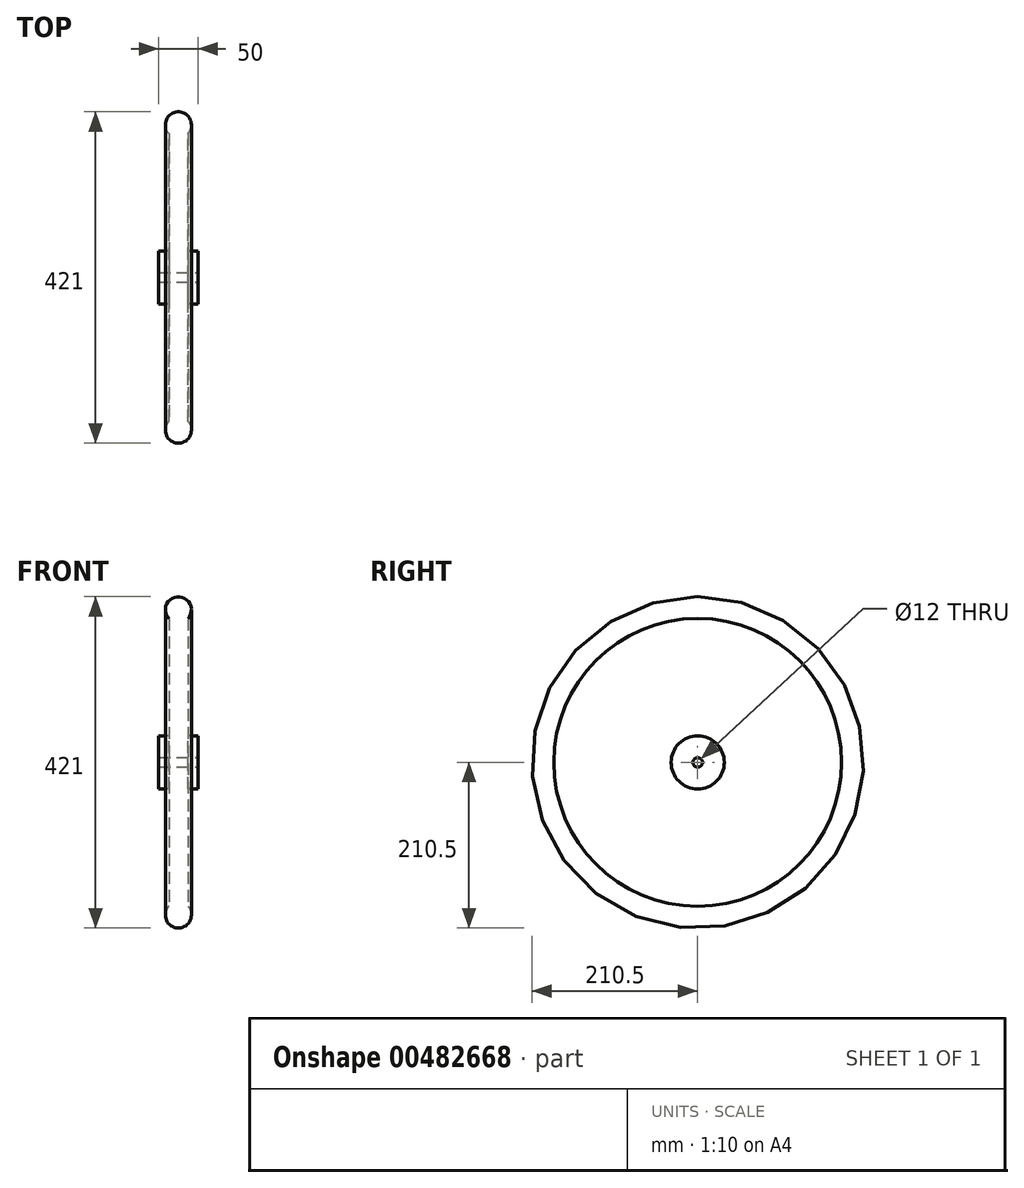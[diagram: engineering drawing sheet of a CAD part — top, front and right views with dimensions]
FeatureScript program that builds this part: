
annotation { "Feature Type Name" : "Feature", "Feature Type Description" : "" }
export const myFeature = defineFeature(function(context is Context, id is Id, definition is map)
    precondition{}
    {
        {
            var Q0;
            Q0=qCreatedBy(makeId("Front.planeOp"),FACE);
            var sketch = newSketch(context, id + "F0", { "sketchPlane" : qUnion([Q0])});
            skArc(sketch, "E0", {"start": v(12.11, 182.8) * mm, "mid": v(0, 210.5) * mm, "end": v(-12.11, 182.8) * mm});
            skLineSegment(sketch, "E1.top", {"start": v(-12.11, 0) * mm, "end": v(12.11, 0) * mm});
            skLineSegment(sketch, "E1.left", {"start": v(-12.11, 182.8) * mm, "end": v(-12.11, 0) * mm});
            skLineSegment(sketch, "E1.right", {"start": v(12.11, 182.8) * mm, "end": v(12.11, 0) * mm});
            skSolve(sketch);
        }
        {
            var Q0;
            Q0=makeQuery(id+"F0.imprint","IMPRINT",FACE,{"disambiguationData":[TD([[makeQuery(id+"F0.imprint","IMPRINT",EDGE,{"derivedFrom":sQuery(id+"F0.wireOp",EDGE,"E0")}),1.0]])]});
            var Q1;
            Q1=sQuery(id+"F0.wireOp",EDGE,"E1.top");
            revolve(context, id + "F1", {"entities" : qUnion([Q0]), "axis" : qUnion([Q1]), "revolveType" : RevolveType.FULL});
        }
        {
            var Q0;
            Q0=makeQuery(id+"F1.opRevolve","SWEPT_FACE",FACE,{"disambiguationData":[OSD([sQuery(id+"F0.wireOp",EDGE,"E1.right")])]});
            var sketch = newSketch(context, id + "F2", { "sketchPlane" : qUnion([Q0])});
            skCircle(sketch, "E2", {"center": v(0, 0) * mm, "radius": 6 * mm});
            skSolve(sketch);
        }
        {
            var Q0;
            Q0 = qSketchRegion(id + "F2", true);
            extrude(context, id + "F3", {"entities" : qUnion([Q0]), "operationType" : NewBodyOperationType.REMOVE, "oppositeDirection" : true, "depth" : 25 * mm});
        }
        {
            var Q0;
            Q0=qCreatedBy(makeId("Right.planeOp"),FACE);
            var sketch = newSketch(context, id + "F4", { "sketchPlane" : qUnion([Q0])});
            skCircle(sketch, "E3", {"center": v(0, 0) * mm, "radius": 33.74 * mm});
            skCircle(sketch, "E4", {"center": v(0, 0) * mm, "radius": 6 * mm});
            skSolve(sketch);
        }
        {
            var Q0;
            Q0 = qSketchRegion(id + "F4", true);
            extrude(context, id + "F5", {"entities" : qUnion([Q0]), "operationType" : NewBodyOperationType.ADD, "depth" : 50 * mm, "symmetric" : true});
        }
    });
